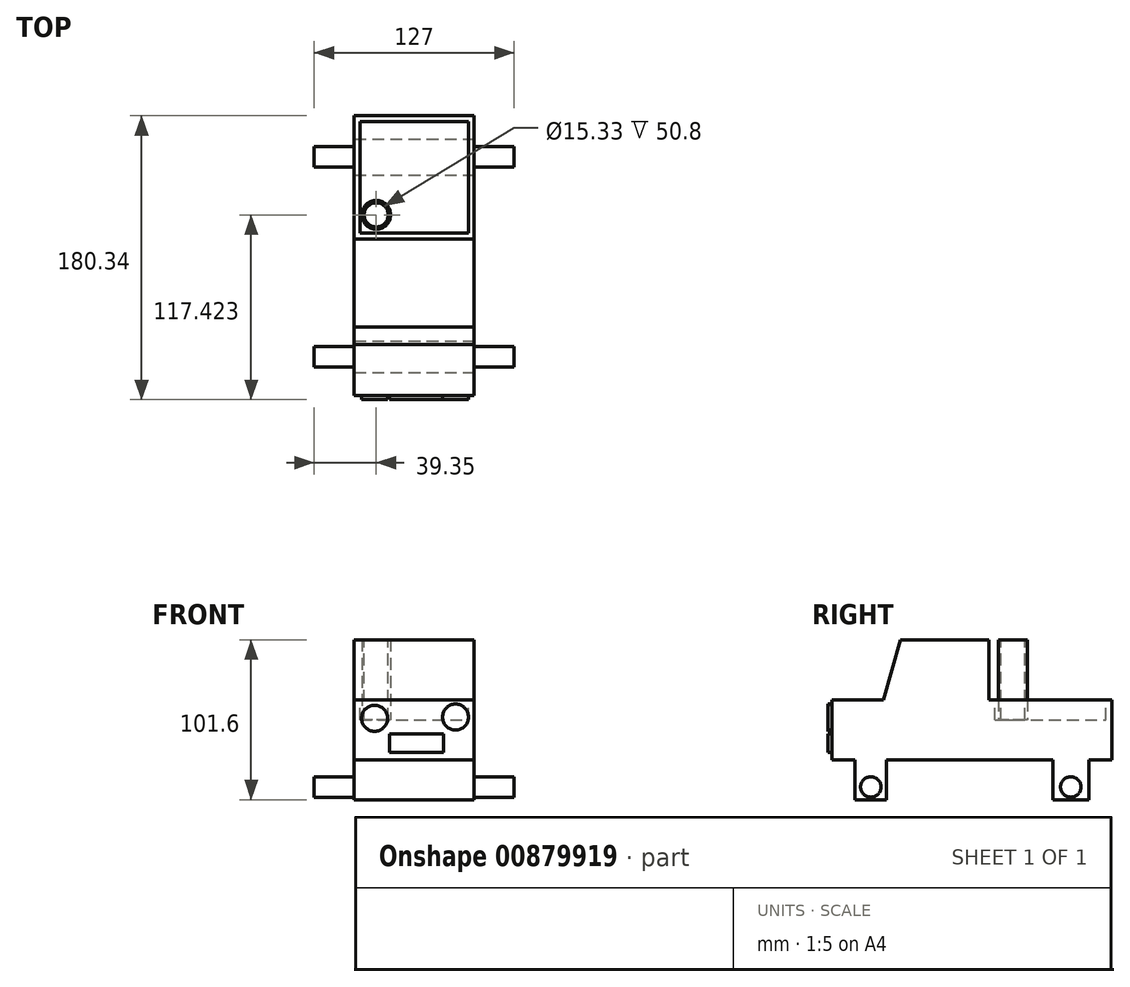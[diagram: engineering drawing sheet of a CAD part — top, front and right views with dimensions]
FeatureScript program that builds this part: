
annotation { "Feature Type Name" : "Feature", "Feature Type Description" : "" }
export const myFeature = defineFeature(function(context is Context, id is Id, definition is map)
    precondition{}
    {
        {
            var Q0;
            Q0=qCreatedBy(makeId("Right.planeOp"),FACE);
            var sketch = newSketch(context, id + "F0", { "sketchPlane" : qUnion([Q0])});
            skLineSegment(sketch, "E0.bottom", {"start": v(-38.38, 16.43) * mm, "end": v(139.42, 16.43) * mm});
            skLineSegment(sketch, "E0.top", {"start": v(-38.38, -21.67) * mm, "end": v(139.42, -21.67) * mm});
            skLineSegment(sketch, "E0.left", {"start": v(-38.38, 16.43) * mm, "end": v(-38.38, -21.67) * mm});
            skLineSegment(sketch, "E0.right", {"start": v(139.42, 16.43) * mm, "end": v(139.42, -21.67) * mm});
            skSolve(sketch);
        }
        {
            var Q0;
            Q0 = qSketchRegion(id + "F0", true);
            extrude(context, id + "F1", {"entities" : qUnion([Q0]), "depth" : 76.2 * mm, "offsetDistance" : 25.4 * mm});
        }
        {
            var Q0;
            Q0=makeQuery(id+"F1.opExtrude","SWEPT_FACE",FACE,{"disambiguationData":[OSD([sQuery(id+"F0.wireOp",EDGE,"E0.bottom")])]});
            var sketch = newSketch(context, id + "F2", { "sketchPlane" : qUnion([Q0])});
            skLineSegment(sketch, "E1.bottom", {"start": v(0, -5.74) * mm, "end": v(76.2, -5.74) * mm});
            skLineSegment(sketch, "E1.top", {"start": v(0, 61.12) * mm, "end": v(76.2, 61.12) * mm});
            skLineSegment(sketch, "E1.left", {"start": v(0, -5.74) * mm, "end": v(0, 61.12) * mm});
            skLineSegment(sketch, "E1.right", {"start": v(76.2, -5.74) * mm, "end": v(76.2, 61.12) * mm});
            skSolve(sketch);
        }
        {
            var Q0;
            Q0 = qSketchRegion(id + "F2", true);
            extrude(context, id + "F3", {"entities" : qUnion([Q0]), "operationType" : NewBodyOperationType.ADD, "depth" : 38.1 * mm, "offsetDistance" : 25.4 * mm});
        }
        {
            var Q0;
            Q0=makeQuery(id+"F3.boolean.opBoolean","MERGE",FACE,{"derivedFrom":[makeQuery(id+"F1.opExtrude","CAP_FACE",FACE,{"disambiguationData":[OSD([sQuery(id+"F0.wireOp",EDGE,"E0.bottom"),sQuery(id+"F0.wireOp",EDGE,"E0.top"),sQuery(id+"F0.wireOp",EDGE,"E0.left"),sQuery(id+"F0.wireOp",EDGE,"E0.right")])],"isStart":false}),makeQuery(id+"F3.opExtrude","SWEPT_FACE",FACE,{"disambiguationData":[OSD([sQuery(id+"F2.wireOp",EDGE,"E1.right")])]})]});
            var sketch = newSketch(context, id + "F4", { "sketchPlane" : qUnion([Q0])});
            skLineSegment(sketch, "E2", {"start": v(-5.74, 16.43) * mm, "end": v(5.23, 54.53) * mm});
            skSolve(sketch);
        }
        {
            var Q0;
            {var subQ0=sQuery(id+"F4.wireOp",EDGE,"E2");Q0=makeQuery(id+"F4.imprint","IMPRINT",FACE,{"disambiguationData":[TD([[makeQuery(id+"F4.imprint","IMPRINT",EDGE,{"derivedFrom":subQ0}),1.0]])]});}
            extrude(context, id + "F5", {"entities" : qUnion([Q0]), "operationType" : NewBodyOperationType.REMOVE, "oppositeDirection" : true, "depth" : 101.6 * mm, "offsetDistance" : 25.4 * mm});
        }
        {
            var Q0;
            Q0=makeQuery(id+"F1.opExtrude","SWEPT_FACE",FACE,{"disambiguationData":[OSD([sQuery(id+"F0.wireOp",EDGE,"E0.left")])]});
            var sketch = newSketch(context, id + "F6", { "sketchPlane" : qUnion([Q0])});
            skCircle(sketch, "E3", {"center": v(12.9, 4.62) * mm, "radius": 8.26 * mm});
            skCircle(sketch, "E4", {"center": v(64.32, 5.44) * mm, "radius": 8.26 * mm});
            skLineSegment(sketch, "E5.bottom", {"start": v(22.3, -5.18) * mm, "end": v(56.71, -5.18) * mm});
            skLineSegment(sketch, "E5.top", {"start": v(22.3, -16.93) * mm, "end": v(56.71, -16.93) * mm});
            skLineSegment(sketch, "E5.left", {"start": v(22.3, -5.18) * mm, "end": v(22.3, -16.93) * mm});
            skLineSegment(sketch, "E5.right", {"start": v(56.71, -5.18) * mm, "end": v(56.71, -16.93) * mm});
            skSolve(sketch);
        }
        {
            var Q0;
            Q0 = qSketchRegion(id + "F6", true);
            extrude(context, id + "F7", {"entities" : qUnion([Q0]), "operationType" : NewBodyOperationType.ADD, "depth" : 2.54 * mm, "offsetDistance" : 25.4 * mm});
        }
        {
            var Q0;
            {var subQ0=sQuery(id+"F0.wireOp",EDGE,"E0.right");var subQ3=sQuery(id+"F0.wireOp",EDGE,"E0.bottom");Q0=makeQuery(id+"F3.boolean.opBoolean","SPLIT",FACE,{"disambiguationData":[TD([makeQuery(id+"F1.opExtrude","SWEPT_FACE",FACE,{"disambiguationData":[OSD([subQ0])]})])],"derivedFrom":makeQuery(id+"F1.opExtrude","SWEPT_FACE",FACE,{"disambiguationData":[OSD([subQ3])]})});}
            var sketch = newSketch(context, id + "F8", { "sketchPlane" : qUnion([Q0])});
            skLineSegment(sketch, "E6.bottom", {"start": v(3.56, 64.93) * mm, "end": v(72.64, 64.93) * mm});
            skLineSegment(sketch, "E6.top", {"start": v(3.56, 135.61) * mm, "end": v(72.64, 135.61) * mm});
            skLineSegment(sketch, "E6.left", {"start": v(3.56, 64.93) * mm, "end": v(3.56, 135.61) * mm});
            skLineSegment(sketch, "E6.right", {"start": v(72.64, 64.93) * mm, "end": v(72.64, 135.61) * mm});
            skSolve(sketch);
        }
        {
            var Q0;
            Q0 = qSketchRegion(id + "F8", true);
            extrude(context, id + "F9", {"entities" : qUnion([Q0]), "operationType" : NewBodyOperationType.REMOVE, "oppositeDirection" : true, "depth" : 12.7 * mm, "offsetDistance" : 25.4 * mm});
        }
        {
            var Q0;
            Q0=makeQuery(id+"F9.boolean.opBoolean","COPY",FACE,{"derivedFrom":makeQuery(id+"F9.opExtrude","CAP_FACE",FACE,{"disambiguationData":[OSD([sQuery(id+"F8.wireOp",EDGE,"E6.bottom"),sQuery(id+"F8.wireOp",EDGE,"E6.top"),sQuery(id+"F8.wireOp",EDGE,"E6.left"),sQuery(id+"F8.wireOp",EDGE,"E6.right")])],"isStart":false})});
            var sketch = newSketch(context, id + "F10", { "sketchPlane" : qUnion([Q0])});
            skCircle(sketch, "E7", {"center": v(13.95, 76.5) * mm, "radius": 9.1 * mm});
            skSolve(sketch);
        }
        {
            var Q0;
            Q0 = qSketchRegion(id + "F10", true);
            extrude(context, id + "F11", {"entities" : qUnion([Q0]), "operationType" : NewBodyOperationType.ADD, "depth" : 50.8 * mm, "offsetDistance" : 25.4 * mm});
        }
        {
            var Q0;
            Q0=makeQuery(id+"F11.opExtrude","CAP_FACE",FACE,{"disambiguationData":[OSD([sQuery(id+"F10.wireOp",EDGE,"E7")])],"isStart":false});
            var sketch = newSketch(context, id + "F12", { "sketchPlane" : qUnion([Q0])});
            skCircle(sketch, "E8", {"center": v(13.95, 76.5) * mm, "radius": 7.66 * mm});
            skSolve(sketch);
        }
        {
            var Q0;
            Q0 = qSketchRegion(id + "F12", true);
            extrude(context, id + "F13", {"entities" : qUnion([Q0]), "operationType" : NewBodyOperationType.REMOVE, "oppositeDirection" : true, "depth" : 50.8 * mm, "offsetDistance" : 25.4 * mm});
        }
        {
            var Q0;
            Q0=makeQuery(id+"F1.opExtrude","SWEPT_FACE",FACE,{"disambiguationData":[OSD([sQuery(id+"F0.wireOp",EDGE,"E0.top")])]});
            var sketch = newSketch(context, id + "F14", { "sketchPlane" : qUnion([Q0])});
            skLineSegment(sketch, "E9.bottom", {"start": v(0, -101.83) * mm, "end": v(76.2, -101.83) * mm});
            skLineSegment(sketch, "E9.top", {"start": v(0, -124.68) * mm, "end": v(76.2, -124.68) * mm});
            skLineSegment(sketch, "E9.left", {"start": v(0, -101.83) * mm, "end": v(0, -124.68) * mm});
            skLineSegment(sketch, "E9.right", {"start": v(76.2, -101.83) * mm, "end": v(76.2, -124.68) * mm});
            skLineSegment(sketch, "E10.bottom", {"start": v(0, 23.74) * mm, "end": v(76.2, 23.74) * mm});
            skLineSegment(sketch, "E10.top", {"start": v(0, 3.79) * mm, "end": v(76.2, 3.79) * mm});
            skLineSegment(sketch, "E10.left", {"start": v(0, 23.74) * mm, "end": v(0, 3.79) * mm});
            skLineSegment(sketch, "E10.right", {"start": v(76.2, 23.74) * mm, "end": v(76.2, 3.79) * mm});
            skSolve(sketch);
        }
        {
            var Q0;
            Q0 = qSketchRegion(id + "F14", true);
            extrude(context, id + "F15", {"entities" : qUnion([Q0]), "operationType" : NewBodyOperationType.ADD, "depth" : 25.4 * mm, "offsetDistance" : 25.4 * mm});
        }
        {
            var Q0;
            Q0=makeQuery(id+"F15.boolean.opBoolean","MERGE",FACE,{"derivedFrom":[makeQuery(id+"F3.boolean.opBoolean","MERGE",FACE,{"derivedFrom":[makeQuery(id+"F1.opExtrude","CAP_FACE",FACE,{"disambiguationData":[OSD([sQuery(id+"F0.wireOp",EDGE,"E0.bottom"),sQuery(id+"F0.wireOp",EDGE,"E0.top"),sQuery(id+"F0.wireOp",EDGE,"E0.left"),sQuery(id+"F0.wireOp",EDGE,"E0.right")])],"isStart":false}),makeQuery(id+"F3.opExtrude","SWEPT_FACE",FACE,{"disambiguationData":[OSD([sQuery(id+"F2.wireOp",EDGE,"E1.right")])]})]}),makeQuery(id+"F15.opExtrude","SWEPT_FACE",FACE,{"disambiguationData":[OSD([sQuery(id+"F14.wireOp",EDGE,"E9.right")])]}),makeQuery(id+"F15.opExtrude","SWEPT_FACE",FACE,{"disambiguationData":[OSD([sQuery(id+"F14.wireOp",EDGE,"E10.right")])]})]});
            var sketch = newSketch(context, id + "F16", { "sketchPlane" : qUnion([Q0])});
            skCircle(sketch, "E11", {"center": v(-13.76, -38.97) * mm, "radius": 6.48 * mm});
            skPoint(sketch, "E11.centerSnap0", {"position": v(-13.76, -47.07) * mm});
            skCircle(sketch, "E12", {"center": v(113.26, -38.97) * mm, "radius": 6.48 * mm});
            skPoint(sketch, "E12.centerSnap0", {"position": v(113.26, -47.07) * mm});
            skSolve(sketch);
        }
        {
            var Q0;
            Q0 = qSketchRegion(id + "F16", true);
            extrude(context, id + "F17", {"entities" : qUnion([Q0]), "operationType" : NewBodyOperationType.ADD, "depth" : 25.4 * mm, "offsetDistance" : 25.4 * mm});
        }
        {
            var Q0;
            Q0=makeQuery(id+"F15.boolean.opBoolean","MERGE",FACE,{"derivedFrom":[makeQuery(id+"F3.boolean.opBoolean","MERGE",FACE,{"derivedFrom":[makeQuery(id+"F1.opExtrude","CAP_FACE",FACE,{"disambiguationData":[OSD([sQuery(id+"F0.wireOp",EDGE,"E0.bottom"),sQuery(id+"F0.wireOp",EDGE,"E0.top"),sQuery(id+"F0.wireOp",EDGE,"E0.left"),sQuery(id+"F0.wireOp",EDGE,"E0.right")])],"isStart":true}),makeQuery(id+"F3.opExtrude","SWEPT_FACE",FACE,{"disambiguationData":[OSD([sQuery(id+"F2.wireOp",EDGE,"E1.left")])]})]}),makeQuery(id+"F15.opExtrude","SWEPT_FACE",FACE,{"disambiguationData":[OSD([sQuery(id+"F14.wireOp",EDGE,"E9.left")])]}),makeQuery(id+"F15.opExtrude","SWEPT_FACE",FACE,{"disambiguationData":[OSD([sQuery(id+"F14.wireOp",EDGE,"E10.left")])]})]});
            var sketch = newSketch(context, id + "F18", { "sketchPlane" : qUnion([Q0])});
            skCircle(sketch, "E13", {"center": v(-113.26, -38.97) * mm, "radius": 6.48 * mm});
            skPoint(sketch, "E13.centerSnap0", {"position": v(-113.26, -47.07) * mm});
            skCircle(sketch, "E14", {"center": v(13.76, -38.97) * mm, "radius": 6.48 * mm});
            skPoint(sketch, "E14.centerSnap0", {"position": v(13.76, -47.07) * mm});
            skSolve(sketch);
        }
        {
            var Q0;
            Q0 = qSketchRegion(id + "F18", true);
            extrude(context, id + "F19", {"entities" : qUnion([Q0]), "operationType" : NewBodyOperationType.ADD, "depth" : 25.4 * mm, "offsetDistance" : 25.4 * mm});
        }
    });
